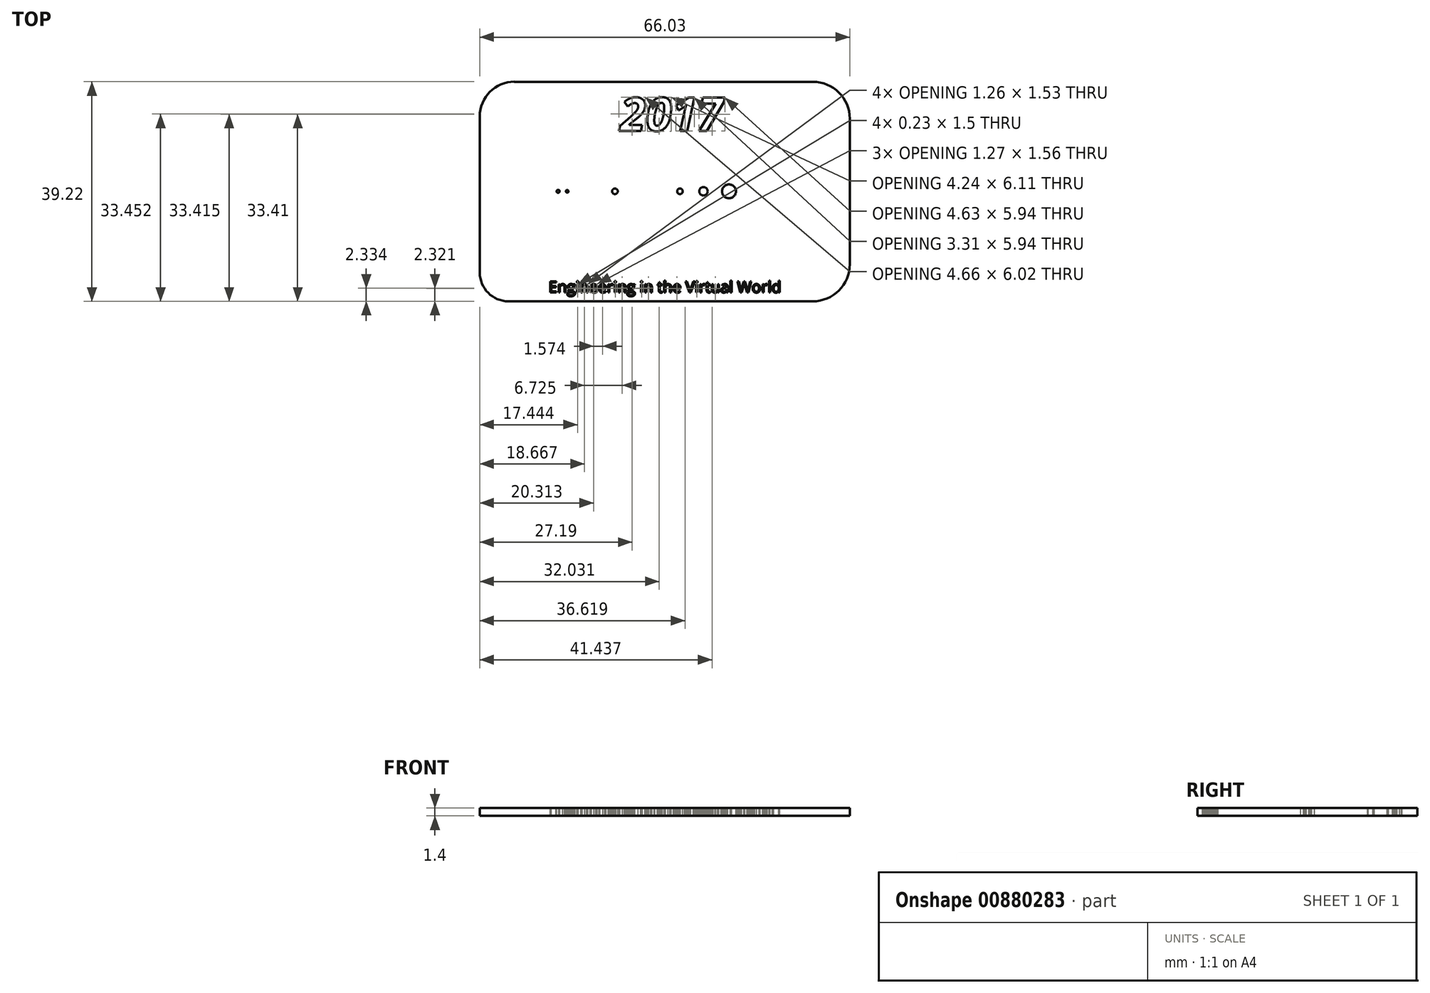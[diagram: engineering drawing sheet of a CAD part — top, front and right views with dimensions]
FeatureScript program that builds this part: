
annotation { "Feature Type Name" : "Feature", "Feature Type Description" : "" }
export const myFeature = defineFeature(function(context is Context, id is Id, definition is map)
    precondition{}
    {
        {
            var Q0;
            Q0=qCreatedBy(makeId("Top.planeOp"),FACE);
            var sketch = newSketch(context, id + "F0", { "sketchPlane" : qUnion([Q0])});
            skCircle(sketch, "E0", {"center": v(0, 0) * mm, "radius": 1.24 * mm});
            skCircle(sketch, "E1", {"center": v(-4.56, 0) * mm, "radius": 0.75 * mm});
            skCircle(sketch, "E2", {"center": v(-8.76, 0) * mm, "radius": 0.5 * mm});
            skCircle(sketch, "E3", {"center": v(-20.37, 0) * mm, "radius": 0.5 * mm});
            skCircle(sketch, "E4", {"center": v(-28.89, 0) * mm, "radius": 0.23 * mm});
            skCircle(sketch, "E5", {"center": v(-30.5, 0) * mm, "radius": 0.26 * mm});
            skFitSpline(sketch, "E6", {"points": [v(-37.86, 0) * mm, v(-29.65, -1.8) * mm, v(-17.5, -2.24) * mm, v(0, -2.2) * mm, v(1.46, -3.8) * mm, v(2.62, -1.8) * mm, v(12, -0.68) * mm], "startDerivative": vector(46.4, -11.45) * mm, "endDerivative": vector(63.67, -3.45) * mm});
            skFitSpline(sketch, "E7", {"points": [v(-37.86, 0) * mm, v(-35.22, 1.1) * mm, v(-29.65, 2) * mm, v(-17.5, 2.22) * mm, v(0, 2.27) * mm, v(1.46, 4.14) * mm, v(2.62, 1.82) * mm, v(8.07, 0.62) * mm, v(12, 0.75) * mm], "startDerivative": vector(27.22, 13.68) * mm, "endDerivative": vector(34.2, 1.53) * mm});
            skLineSegment(sketch, "E8", {"start": v(12, -0.68) * mm, "end": v(12, 0.75) * mm});
            skSolve(sketch);
        }
        {
            var Q0;
            Q0=qCreatedBy(makeId("Top.planeOp"),FACE);
            var sketch = newSketch(context, id + "F1", { "sketchPlane" : qUnion([Q0])});
            skLineSegment(sketch, "E9.bottom", {"start": v(14.93, -19.65) * mm, "end": v(-39.35, -19.65) * mm});
            skLineSegment(sketch, "E9.top", {"start": v(14.95, 19.57) * mm, "end": v(-38.3, 19.57) * mm});
            skLineSegment(sketch, "E9.left", {"start": v(21.55, -13.03) * mm, "end": v(21.55, 12.98) * mm});
            skLineSegment(sketch, "E9.right", {"start": v(-44.48, -14.52) * mm, "end": v(-44.48, 13.38) * mm});
            skPoint(sketch, "E10.visualSharp", {"position": v(21.55, 19.57) * mm});
            skArc(sketch, "E10.filletArc", {"start": v(21.55, 12.98) * mm, "mid": v(19.62, 17.64) * mm, "end": v(14.95, 19.57) * mm});
            skPoint(sketch, "E11.visualSharp", {"position": v(21.55, -19.65) * mm});
            skArc(sketch, "E11.filletArc", {"start": v(14.93, -19.65) * mm, "mid": v(19.6, -17.71) * mm, "end": v(21.55, -13.03) * mm});
            skPoint(sketch, "E12.visualSharp", {"position": v(-44.48, 19.57) * mm});
            skArc(sketch, "E12.filletArc", {"start": v(-38.3, 19.57) * mm, "mid": v(-42.67, 17.76) * mm, "end": v(-44.48, 13.38) * mm});
            skPoint(sketch, "E13.visualSharp", {"position": v(-44.48, -19.65) * mm});
            skArc(sketch, "E13.filletArc", {"start": v(-44.48, -14.52) * mm, "mid": v(-42.98, -18.15) * mm, "end": v(-39.35, -19.65) * mm});
            skSolve(sketch);
        }
        {
            var Q0;
            Q0=makeQuery(id+"F1.imprint","IMPRINT",FACE,{"disambiguationData":[TD([[makeQuery(id+"F1.imprint","IMPRINT",EDGE,{"derivedFrom":sQuery(id+"F1.wireOp",EDGE,"E9.bottom")}),-1.0]])]});
            extrude(context, id + "F2", {"entities" : qUnion([Q0]), "depth" : 1.4 * mm, "offsetDistance" : 25 * mm});
        }
        {
            var Q0;
            Q0=makeQuery(id+"F0.imprint","IMPRINT",FACE,{"disambiguationData":[TD([[makeQuery(id+"F0.imprint","IMPRINT",EDGE,{"derivedFrom":sQuery(id+"F0.wireOp",EDGE,"E5")}),1.0]])]});
            var Q1;
            Q1=makeQuery(id+"F0.imprint","IMPRINT",FACE,{"disambiguationData":[TD([[makeQuery(id+"F0.imprint","IMPRINT",EDGE,{"derivedFrom":sQuery(id+"F0.wireOp",EDGE,"E4")}),1.0]])]});
            var Q2;
            Q2=makeQuery(id+"F0.imprint","IMPRINT",FACE,{"disambiguationData":[TD([[makeQuery(id+"F0.imprint","IMPRINT",EDGE,{"derivedFrom":sQuery(id+"F0.wireOp",EDGE,"E3")}),1.0]])]});
            var Q3;
            Q3=makeQuery(id+"F0.imprint","IMPRINT",FACE,{"disambiguationData":[TD([[makeQuery(id+"F0.imprint","IMPRINT",EDGE,{"derivedFrom":sQuery(id+"F0.wireOp",EDGE,"E2")}),1.0]])]});
            var Q4;
            Q4=makeQuery(id+"F0.imprint","IMPRINT",FACE,{"disambiguationData":[TD([[makeQuery(id+"F0.imprint","IMPRINT",EDGE,{"derivedFrom":sQuery(id+"F0.wireOp",EDGE,"E1")}),1.0]])]});
            var Q5;
            Q5=makeQuery(id+"F0.imprint","IMPRINT",FACE,{"disambiguationData":[TD([[makeQuery(id+"F0.imprint","IMPRINT",EDGE,{"derivedFrom":sQuery(id+"F0.wireOp",EDGE,"E0")}),1.0]])]});
            extrude(context, id + "F3", {"entities" : qUnion([Q0, Q1, Q2, Q3, Q4, Q5]), "operationType" : NewBodyOperationType.REMOVE, "oppositeDirection" : true, "depth" : 25 * mm, "offsetDistance" : 25 * mm, "hasSecondDirection" : true, "secondDirectionOppositeDirection" : false, "secondDirectionDepth" : 25 * mm});
        }
        {
            var Q0;
            Q0=makeQuery(id+"F2.opExtrude","CAP_FACE",FACE,{"disambiguationData":[OSD([sQuery(id+"F1.wireOp",EDGE,"E9.bottom"),sQuery(id+"F1.wireOp",EDGE,"E9.top"),sQuery(id+"F1.wireOp",EDGE,"E9.left"),sQuery(id+"F1.wireOp",EDGE,"E9.right"),sQuery(id+"F1.wireOp",EDGE,"E10.filletArc"),sQuery(id+"F1.wireOp",EDGE,"E11.filletArc"),sQuery(id+"F1.wireOp",EDGE,"E12.filletArc"),sQuery(id+"F1.wireOp",EDGE,"E13.filletArc")])],"isStart":false});
            var sketch = newSketch(context, id + "F4", { "sketchPlane" : qUnion([Q0])});
            skText(sketch, "E14", { "text": "2017", "fontName": "OpenSans-BoldItalic.ttf"});
            const initialGuessF4  = {"E14": [-0.01942, 0.01079, 1, 0, 0.00599]};
            skSetInitialGuess(sketch, initialGuessF4);
            skSolve(sketch);
        }
        {
            var Q0;
            Q0 = qSketchRegion(id + "F4", true);
            extrude(context, id + "F5", {"entities" : qUnion([Q0]), "operationType" : NewBodyOperationType.REMOVE, "oppositeDirection" : true, "depth" : 25 * mm, "offsetDistance" : 25 * mm, "hasSecondDirection" : true, "secondDirectionOppositeDirection" : false, "secondDirectionDepth" : 25 * mm});
        }
        {
            var Q0;
            {var subQ0=sQuery(id+"F1.wireOp",EDGE,"E13.filletArc");var subQ1=sQuery(id+"F1.wireOp",EDGE,"E9.bottom");var subQ2=sQuery(id+"F1.wireOp",EDGE,"E12.filletArc");var subQ3=sQuery(id+"F1.wireOp",EDGE,"E9.top");var subQ4=sQuery(id+"F1.wireOp",EDGE,"E9.left");var subQ5=sQuery(id+"F1.wireOp",EDGE,"E9.right");var subQ6=sQuery(id+"F1.wireOp",EDGE,"E10.filletArc");var subQ7=sQuery(id+"F1.wireOp",EDGE,"E11.filletArc");Q0=makeQuery(id+"F5.boolean.opBoolean","SPLIT",FACE,{"disambiguationData":[TD([makeQuery(id+"F2.opExtrude","SWEPT_FACE",FACE,{"disambiguationData":[OSD([subQ1])]})])],"derivedFrom":makeQuery(id+"F2.opExtrude","CAP_FACE",FACE,{"disambiguationData":[OSD([subQ1,subQ3,subQ4,subQ5,subQ6,subQ7,subQ2,subQ0])],"isStart":false})});}
            var sketch = newSketch(context, id + "F6", { "sketchPlane" : qUnion([Q0])});
            skText(sketch, "E15", { "text": "Engineering in the Virtual World", "fontName": "OpenSans-Regular.ttf"});
            const initialGuessF6  = {"E15": [-0.03221, -0.01808, 1, 0, 0.00202]};
            skSetInitialGuess(sketch, initialGuessF6);
            skSolve(sketch);
        }
        {
            var Q0;
            Q0 = qSketchRegion(id + "F6", true);
            extrude(context, id + "F7", {"entities" : qUnion([Q0]), "operationType" : NewBodyOperationType.REMOVE, "oppositeDirection" : true, "depth" : 25 * mm, "offsetDistance" : 25 * mm, "hasSecondDirection" : true, "secondDirectionOppositeDirection" : false, "secondDirectionDepth" : 25 * mm});
        }
    });
